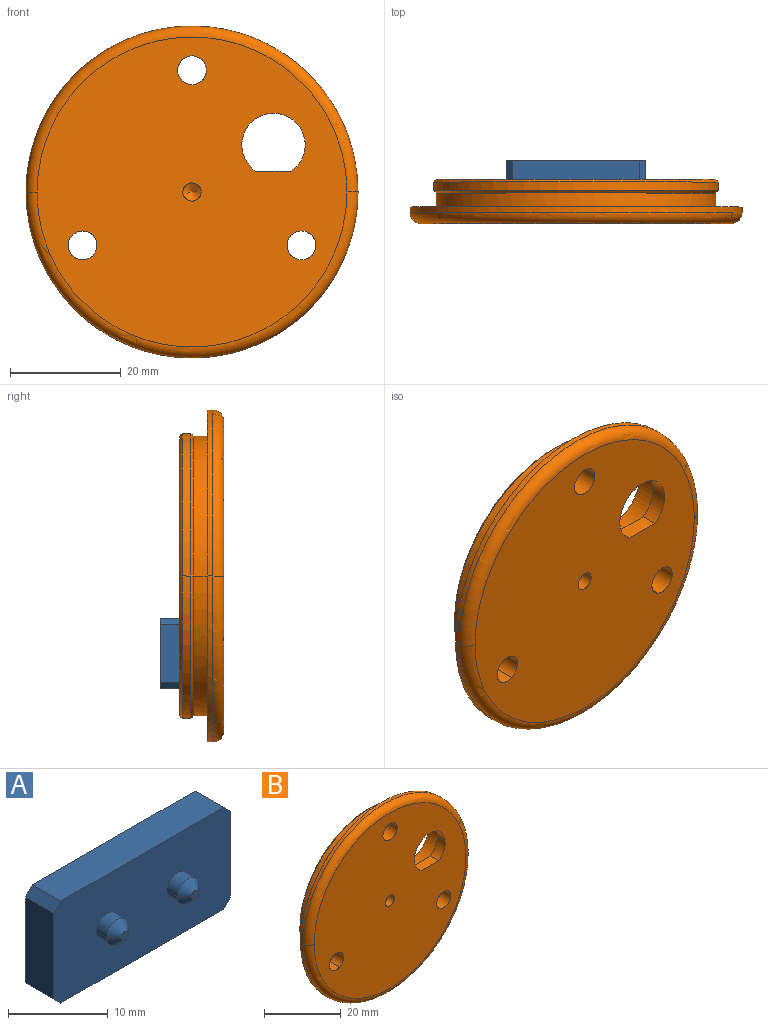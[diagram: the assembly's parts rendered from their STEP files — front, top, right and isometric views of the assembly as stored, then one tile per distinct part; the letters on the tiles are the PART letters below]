
ASSEMBLY  parts=2 mates=1
PART A: 20 faces, bbox 25x6.5x12.5 mm
  f0: plane 1x1mm, normal (0,-1,0), area 0.8mm2, adj f3,f4
  f1: plane 1x1mm, normal (0,-1,0), area 0.8mm2, adj f5,f6
  f2: plane 25x12.5mm, normal (0,1,0), area 310.5mm2, adj f7,f8,f9,f10,f11,f12,f13,f14
  f3: cone r=0mm half-angle=45deg, axis (0,1,0), area 4.4mm2, adj f0,f4,f15
  f4: cone r=0mm half-angle=45deg, axis (0,1,0), area 4.4mm2, adj f0,f3,f16
  f5: cone r=0mm half-angle=45deg, axis (0,1,0), area 4.4mm2, adj f1,f6,f17
  f6: cone r=0mm half-angle=45deg, axis (0,1,0), area 4.4mm2, adj f1,f5,f18
  f7: plane 4x1mm, normal (-0.71,0,0.71), area 5.7mm2, adj f2,f8,f14,f19
  f8: plane 23x4mm, normal (0,0,1), area 92mm2, adj f2,f7,f9,f19
  f9: plane 4x1mm, normal (0.71,0,0.71), area 5.7mm2, adj f2,f8,f10,f19
  f10: plane 10.5x4mm, normal (1,0,0), area 42mm2, adj f2,f9,f11,f19
  f11: plane 4x1mm, normal (0.71,0,-0.71), area 5.7mm2, adj f2,f10,f12,f19
  f12: plane 23x4mm, normal (0,0,-1), area 92mm2, adj f2,f11,f13,f19
  f13: plane 4x1mm, normal (-0.71,0,-0.71), area 5.7mm2, adj f2,f12,f14,f19
  f14: plane 10.5x4mm, normal (-1,0,0), area 42mm2, adj f2,f7,f13,f19
  f15: cylinder r=1.5mm len=3mm, axis (0,-1,0), area 7.1mm2, adj f3,f16,f19
  f16: cylinder r=1.5mm len=3mm, axis (0,-1,0), area 7.1mm2, adj f4,f15,f19
  f17: cylinder r=1.5mm len=3mm, axis (0,-1,0), area 7.1mm2, adj f5,f18,f19
  f18: cylinder r=1.5mm len=3mm, axis (0,-1,0), area 7.1mm2, adj f6,f17,f19
  f19: plane 25x12.5mm, normal (0,-1,0), area 296.4mm2, adj f7,f8,f9,f10,f11,f12,f13,f14
PART B: 37 faces, bbox 64.9x8x64.9 mm
  f0: cone r=0mm half-angle=45deg, axis (0,1,0), area 56.6mm2, adj f1,f3,f4
  f1: cone r=0mm half-angle=45deg, axis (0,1,0), area 56.6mm2, adj f0,f2,f5
  f2: cylinder r=25.25mm len=50.5mm, axis (0,-1,0), area 198.3mm2, adj f1,f3,f8
  f3: cylinder r=25.25mm len=50.5mm, axis (0,-1,0), area 198.3mm2, adj f0,f2,f8
  f4: cylinder r=25.75mm len=51.5mm, axis (0,1,0), area 121.3mm2, adj f0,f5,f9
  f5: cylinder r=25.75mm len=51.5mm, axis (0,1,0), area 121.3mm2, adj f1,f4,f10
  f6: plane 3.03x3mm, normal (0,1,0), area 7.1mm2, adj f11,f12
  f7: plane 3.03x3mm, normal (0,1,0), area 7.1mm2, adj f13,f14
  f8: plane 60.1x60mm, normal (0,1,0), area 824.5mm2, adj f2,f3,f17,f18
  f9: cone r=0mm half-angle=45deg, axis (0,-1,0), area 56.6mm2, adj f4,f10,f19
  f10: cone r=0mm half-angle=45deg, axis (0,-1,0), area 56.6mm2, adj f5,f9,f19
  f11: cylinder r=1.5mm len=3mm, axis (0,1,0), area 14.1mm2, adj f6,f12,f19
  f12: cylinder r=1.5mm len=3mm, axis (0,1,0), area 14.1mm2, adj f6,f11,f19
  f13: cylinder r=1.5mm len=3mm, axis (0,1,0), area 14.1mm2, adj f7,f14,f19
  f14: cylinder r=1.5mm len=3mm, axis (0,1,0), area 14.1mm2, adj f7,f13,f19
  f15: cylinder r=7.5mm len=15mm, axis (0,-1,0), area 117.8mm2, adj f16,f19,f20
  f16: cylinder r=7.5mm len=15mm, axis (0,-1,0), area 117.8mm2, adj f15,f19,f20
  f17: cylinder r=30mm len=60mm, axis (0,1,0), area 94.2mm2, adj f8,f18,f23
  f18: cylinder r=30mm len=60mm, axis (0,1,0), area 94.2mm2, adj f8,f17,f24
  f19: plane 50.59x50.5mm, normal (0,1,0), area 1748.4mm2, adj f9,f10,f11,f12,f13,f14,f15,f16
  f20: plane 15.05x15mm, normal (0,1,0), area 78.1mm2, adj f15,f16,f31,f32,f33
  f21: cone r=0mm half-angle=59deg, axis (0,-1,0), area 5mm2, adj f22,f34
  f22: cone r=0mm half-angle=59deg, axis (0,-1,0), area 5mm2, adj f21,f35
  f23: torus R=28mm, axis (0,1,0), area 288.9mm2, adj f17,f24,f36
  f24: torus R=28mm, axis (0,1,0), area 288.9mm2, adj f18,f23,f36
  f25: cylinder r=2.6mm len=8mm, axis (0,-1,0), area 65.3mm2, adj f19,f26,f36
  f26: cylinder r=2.6mm len=8mm, axis (0,-1,0), area 65.3mm2, adj f19,f25,f36
  f27: cylinder r=2.6mm len=8mm, axis (0,-1,0), area 65.3mm2, adj f19,f28,f36
  f28: cylinder r=2.6mm len=8mm, axis (0,-1,0), area 65.3mm2, adj f19,f27,f36
  f29: cylinder r=2.6mm len=8mm, axis (0,-1,0), area 65.3mm2, adj f19,f30,f36
  f30: cylinder r=2.6mm len=8mm, axis (0,-1,0), area 65.3mm2, adj f19,f29,f36
  f31: plane 6.47x3mm, normal (0,0,1), area 19.4mm2, adj f20,f32,f33,f36
  f32: cylinder r=5.72mm len=4.73mm, axis (0,-1,0), area 16.7mm2, adj f20,f31,f33,f36
  f33: cylinder r=5.72mm len=11.45mm, axis (0,-1,0), area 70.6mm2, adj f20,f31,f32,f36
  f34: cylinder r=1.65mm len=5mm, axis (0,-1,0), area 25.9mm2, adj f21,f35,f36
  f35: cylinder r=1.65mm len=5mm, axis (0,-1,0), area 25.9mm2, adj f22,f34,f36
  f36: plane 56.04x56mm, normal (0,-1,0), area 2292.2mm2, adj f23,f24,f25,f26,f27,f28,f29,f30
PLACE A t=(16.2,0.65,-6.42)mm
PLACE B t=(16.2,-6.85,7.58)mm
MATE fastened A.f5 <-> B.f13  axis (0,-1,0) through (21.2,-1.85,-6.42)mm
